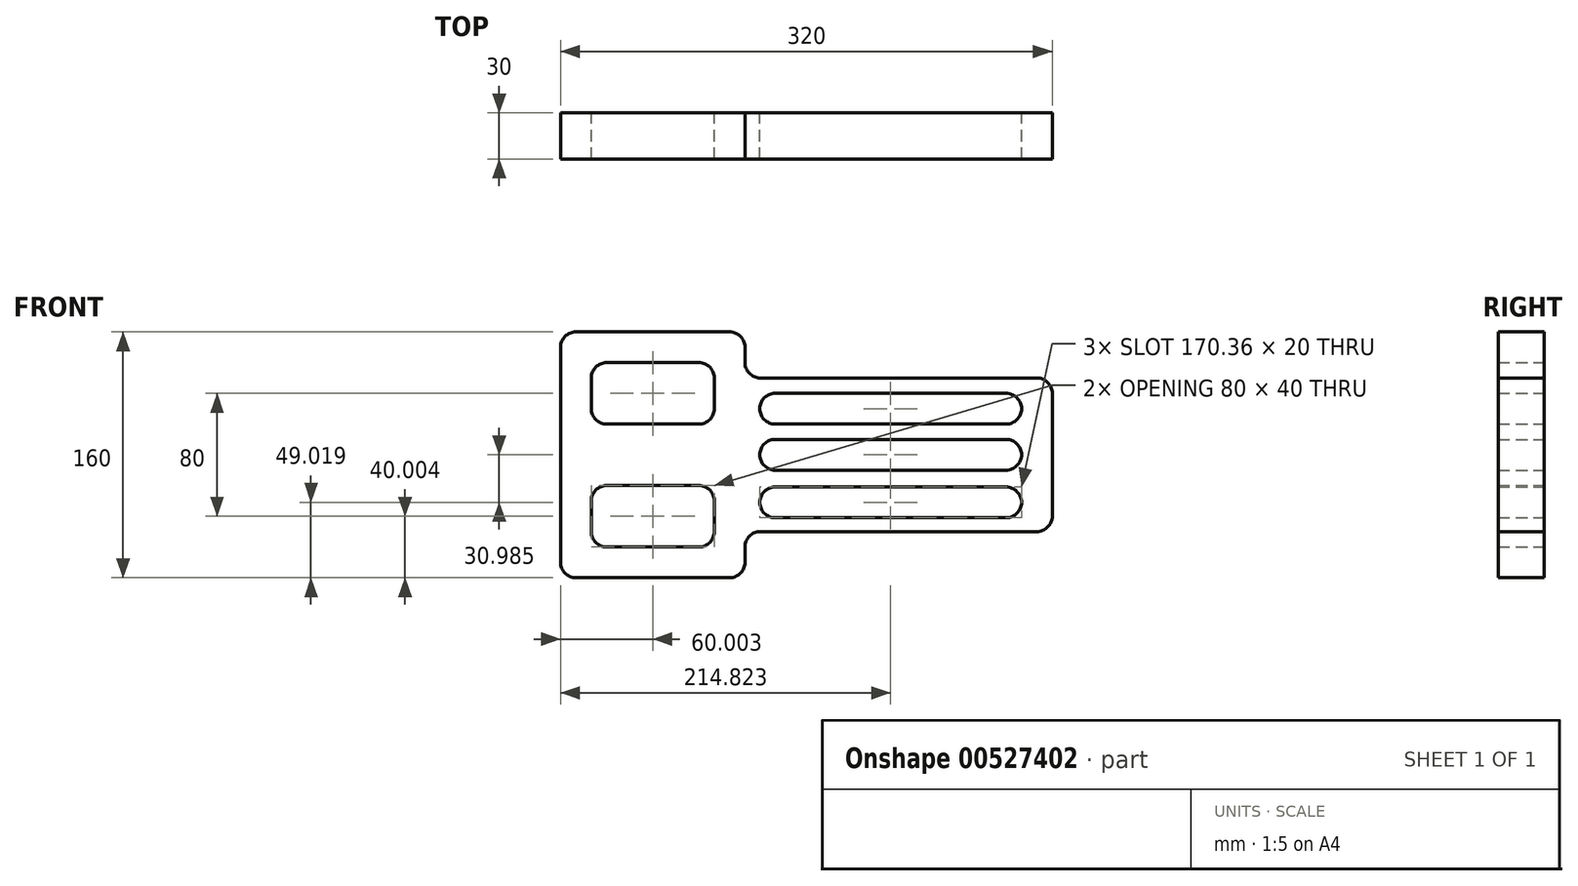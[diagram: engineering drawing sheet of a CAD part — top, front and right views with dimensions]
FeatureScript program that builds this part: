
annotation { "Feature Type Name" : "Feature", "Feature Type Description" : "" }
export const myFeature = defineFeature(function(context is Context, id is Id, definition is map)
    precondition{}
    {
        {
            var Q0;
            Q0=qCreatedBy(makeId("Front.planeOp"),FACE);
            var sketch = newSketch(context, id + "F0", { "sketchPlane" : qUnion([Q0])});
            skLineSegment(sketch, "E0.bottom", {"start": v(-119.76, 63.26) * mm, "end": v(-19.76, 63.26) * mm});
            skLineSegment(sketch, "E0.top", {"start": v(-119.76, -96.74) * mm, "end": v(-19.76, -96.74) * mm});
            skLineSegment(sketch, "E0.left", {"start": v(-129.76, 53.26) * mm, "end": v(-129.76, -86.74) * mm});
            skLineSegment(sketch, "E0.right", {"start": v(-9.76, 53.26) * mm, "end": v(-9.76, 43.26) * mm});
            skLineSegment(sketch, "E1.bottom", {"start": v(-99.76, 43.26) * mm, "end": v(-39.76, 43.26) * mm});
            skLineSegment(sketch, "E1.top", {"start": v(-99.76, 3.26) * mm, "end": v(-39.76, 3.26) * mm});
            skLineSegment(sketch, "E1.left", {"start": v(-109.76, 33.26) * mm, "end": v(-109.76, 13.26) * mm});
            skLineSegment(sketch, "E1.right", {"start": v(-29.76, 33.26) * mm, "end": v(-29.76, 13.26) * mm});
            skLineSegment(sketch, "E2.bottom", {"start": v(-99.76, -36.74) * mm, "end": v(-39.76, -36.74) * mm});
            skLineSegment(sketch, "E2.top", {"start": v(-99.76, -76.74) * mm, "end": v(-39.76, -76.74) * mm});
            skLineSegment(sketch, "E2.left", {"start": v(-109.76, -46.74) * mm, "end": v(-109.76, -66.74) * mm});
            skLineSegment(sketch, "E2.right", {"start": v(-29.76, -46.74) * mm, "end": v(-29.76, -66.74) * mm});
            skPoint(sketch, "E3.visualSharp", {"position": v(-109.76, -36.74) * mm});
            skArc(sketch, "E3.filletArc", {"start": v(-99.76, -36.74) * mm, "mid": v(-106.83, -39.66) * mm, "end": v(-109.76, -46.74) * mm});
            skPoint(sketch, "E4.visualSharp", {"position": v(-29.76, -36.74) * mm});
            skArc(sketch, "E4.filletArc", {"start": v(-29.76, -46.74) * mm, "mid": v(-32.69, -39.66) * mm, "end": v(-39.76, -36.74) * mm});
            skPoint(sketch, "E5.visualSharp", {"position": v(-29.76, -76.74) * mm});
            skArc(sketch, "E5.filletArc", {"start": v(-39.76, -76.74) * mm, "mid": v(-32.69, -73.8) * mm, "end": v(-29.76, -66.74) * mm});
            skPoint(sketch, "E6.visualSharp", {"position": v(-109.76, -76.74) * mm});
            skArc(sketch, "E6.filletArc", {"start": v(-109.76, -66.74) * mm, "mid": v(-106.83, -73.8) * mm, "end": v(-99.76, -76.74) * mm});
            skPoint(sketch, "E7.visualSharp", {"position": v(-109.76, 43.26) * mm});
            skArc(sketch, "E7.filletArc", {"start": v(-99.76, 43.26) * mm, "mid": v(-106.83, 40.34) * mm, "end": v(-109.76, 33.26) * mm});
            skPoint(sketch, "E8.visualSharp", {"position": v(-29.76, 43.26) * mm});
            skArc(sketch, "E8.filletArc", {"start": v(-29.76, 33.26) * mm, "mid": v(-32.69, 40.34) * mm, "end": v(-39.76, 43.26) * mm});
            skPoint(sketch, "E9.visualSharp", {"position": v(-29.76, 3.26) * mm});
            skArc(sketch, "E9.filletArc", {"start": v(-39.76, 3.26) * mm, "mid": v(-32.69, 6.2) * mm, "end": v(-29.76, 13.26) * mm});
            skPoint(sketch, "E10.visualSharp", {"position": v(-109.76, 3.26) * mm});
            skArc(sketch, "E10.filletArc", {"start": v(-109.76, 13.26) * mm, "mid": v(-106.83, 6.2) * mm, "end": v(-99.76, 3.26) * mm});
            skPoint(sketch, "E11.visualSharp", {"position": v(-129.76, 63.26) * mm});
            skArc(sketch, "E11.filletArc", {"start": v(-119.76, 63.26) * mm, "mid": v(-126.83, 60.34) * mm, "end": v(-129.76, 53.26) * mm});
            skPoint(sketch, "E12.visualSharp", {"position": v(-9.76, 63.26) * mm});
            skArc(sketch, "E12.filletArc", {"start": v(-9.76, 53.26) * mm, "mid": v(-12.69, 60.34) * mm, "end": v(-19.76, 63.26) * mm});
            skPoint(sketch, "E13.visualSharp", {"position": v(-9.76, -96.74) * mm});
            skArc(sketch, "E13.filletArc", {"start": v(-19.76, -96.74) * mm, "mid": v(-12.69, -93.8) * mm, "end": v(-9.76, -86.74) * mm});
            skPoint(sketch, "E14.visualSharp", {"position": v(-129.76, -96.74) * mm});
            skArc(sketch, "E14.filletArc", {"start": v(-129.76, -86.74) * mm, "mid": v(-126.83, -93.8) * mm, "end": v(-119.76, -96.74) * mm});
            skLineSegment(sketch, "E15.bottom", {"start": v(0.24, 33.26) * mm, "end": v(180.24, 33.26) * mm});
            skLineSegment(sketch, "E15.top", {"start": v(0.24, -66.74) * mm, "end": v(180.24, -66.74) * mm});
            skLineSegment(sketch, "E15.right", {"start": v(190.24, 23.26) * mm, "end": v(190.24, -56.74) * mm});
            skLineSegment(sketch, "E16.trimOffspring", {"start": v(-9.76, -76.74) * mm, "end": v(-9.76, -86.74) * mm});
            skPoint(sketch, "E17.visualSharp", {"position": v(-9.76, 33.26) * mm});
            skArc(sketch, "E17.filletArc", {"start": v(-9.76, 43.26) * mm, "mid": v(-6.83, 36.2) * mm, "end": v(0.24, 33.26) * mm});
            skPoint(sketch, "E18.visualSharp", {"position": v(-9.76, -66.74) * mm});
            skArc(sketch, "E18.filletArc", {"start": v(0.24, -66.74) * mm, "mid": v(-6.83, -69.66) * mm, "end": v(-9.76, -76.74) * mm});
            skPoint(sketch, "E19.visualSharp", {"position": v(190.24, 33.26) * mm});
            skArc(sketch, "E19.filletArc", {"start": v(190.24, 23.26) * mm, "mid": v(187.31, 30.34) * mm, "end": v(180.24, 33.26) * mm});
            skPoint(sketch, "E20.visualSharp", {"position": v(190.24, -66.74) * mm});
            skArc(sketch, "E20.filletArc", {"start": v(180.24, -66.74) * mm, "mid": v(187.31, -63.8) * mm, "end": v(190.24, -56.74) * mm});
            skLineSegment(sketch, "E21.bottom", {"start": v(9.88, 23.26) * mm, "end": v(160.24, 23.26) * mm});
            skLineSegment(sketch, "E21.top", {"start": v(9.88, 3.26) * mm, "end": v(160.24, 3.26) * mm});
            skLineSegment(sketch, "E21.left", {"start": v(-0.12, 13.26) * mm, "end": v(-0.12, 13.26) * mm});
            skLineSegment(sketch, "E21.right", {"start": v(170.24, 13.26) * mm, "end": v(170.24, 13.26) * mm});
            skLineSegment(sketch, "E22.bottom", {"start": v(9.88, -6.74) * mm, "end": v(160.24, -6.74) * mm});
            skLineSegment(sketch, "E22.top", {"start": v(9.88, -26.74) * mm, "end": v(160.24, -26.74) * mm});
            skLineSegment(sketch, "E22.left", {"start": v(-0.12, -16.74) * mm, "end": v(-0.12, -16.74) * mm});
            skLineSegment(sketch, "E22.right", {"start": v(170.24, -16.74) * mm, "end": v(170.24, -16.74) * mm});
            skLineSegment(sketch, "E23.bottom", {"start": v(9.88, -37.72) * mm, "end": v(160.24, -37.72) * mm});
            skLineSegment(sketch, "E23.top", {"start": v(9.88, -57.72) * mm, "end": v(160.24, -57.72) * mm});
            skLineSegment(sketch, "E23.left", {"start": v(-0.12, -47.72) * mm, "end": v(-0.12, -47.72) * mm});
            skLineSegment(sketch, "E23.right", {"start": v(170.24, -47.72) * mm, "end": v(170.24, -47.72) * mm});
            skPoint(sketch, "E24.visualSharp", {"position": v(-0.12, 23.26) * mm});
            skArc(sketch, "E24.filletArc", {"start": v(9.88, 23.26) * mm, "mid": v(2.81, 20.34) * mm, "end": v(-0.12, 13.26) * mm});
            skPoint(sketch, "E25.visualSharp", {"position": v(-0.12, 3.26) * mm});
            skArc(sketch, "E25.filletArc", {"start": v(-0.12, 13.26) * mm, "mid": v(2.81, 6.2) * mm, "end": v(9.88, 3.26) * mm});
            skPoint(sketch, "E26.visualSharp", {"position": v(170.24, 23.26) * mm});
            skArc(sketch, "E26.filletArc", {"start": v(170.24, 13.26) * mm, "mid": v(167.31, 20.34) * mm, "end": v(160.24, 23.26) * mm});
            skPoint(sketch, "E27.visualSharp", {"position": v(170.24, 3.26) * mm});
            skArc(sketch, "E27.filletArc", {"start": v(160.24, 3.26) * mm, "mid": v(167.31, 6.2) * mm, "end": v(170.24, 13.26) * mm});
            skPoint(sketch, "E28.visualSharp", {"position": v(170.24, -6.74) * mm});
            skArc(sketch, "E28.filletArc", {"start": v(170.24, -16.74) * mm, "mid": v(167.31, -9.66) * mm, "end": v(160.24, -6.74) * mm});
            skPoint(sketch, "E29.visualSharp", {"position": v(170.24, -26.74) * mm});
            skArc(sketch, "E29.filletArc", {"start": v(160.24, -26.74) * mm, "mid": v(167.31, -23.8) * mm, "end": v(170.24, -16.74) * mm});
            skPoint(sketch, "E30.visualSharp", {"position": v(-0.12, -6.74) * mm});
            skArc(sketch, "E30.filletArc", {"start": v(9.88, -6.74) * mm, "mid": v(2.81, -9.66) * mm, "end": v(-0.12, -16.74) * mm});
            skPoint(sketch, "E31.visualSharp", {"position": v(-0.12, -26.74) * mm});
            skArc(sketch, "E31.filletArc", {"start": v(-0.12, -16.74) * mm, "mid": v(2.81, -23.8) * mm, "end": v(9.88, -26.74) * mm});
            skPoint(sketch, "E32.visualSharp", {"position": v(-0.12, -37.72) * mm});
            skArc(sketch, "E32.filletArc", {"start": v(9.88, -37.72) * mm, "mid": v(2.81, -40.65) * mm, "end": v(-0.12, -47.72) * mm});
            skPoint(sketch, "E33.visualSharp", {"position": v(-0.12, -57.72) * mm});
            skArc(sketch, "E33.filletArc", {"start": v(-0.12, -47.72) * mm, "mid": v(2.81, -54.8) * mm, "end": v(9.88, -57.72) * mm});
            skPoint(sketch, "E34.visualSharp", {"position": v(170.24, -37.72) * mm});
            skArc(sketch, "E34.filletArc", {"start": v(170.24, -47.72) * mm, "mid": v(167.31, -40.65) * mm, "end": v(160.24, -37.72) * mm});
            skPoint(sketch, "E35.visualSharp", {"position": v(170.24, -57.72) * mm});
            skArc(sketch, "E35.filletArc", {"start": v(160.24, -57.72) * mm, "mid": v(167.31, -54.8) * mm, "end": v(170.24, -47.72) * mm});
            skSolve(sketch);
        }
        {
            var Q0;
            Q0 = qSketchRegion(id + "F0", true);
            extrude(context, id + "F1", {"entities" : qUnion([Q0]), "depth" : 30 * mm, "offsetDistance" : 25 * mm});
        }
    });
